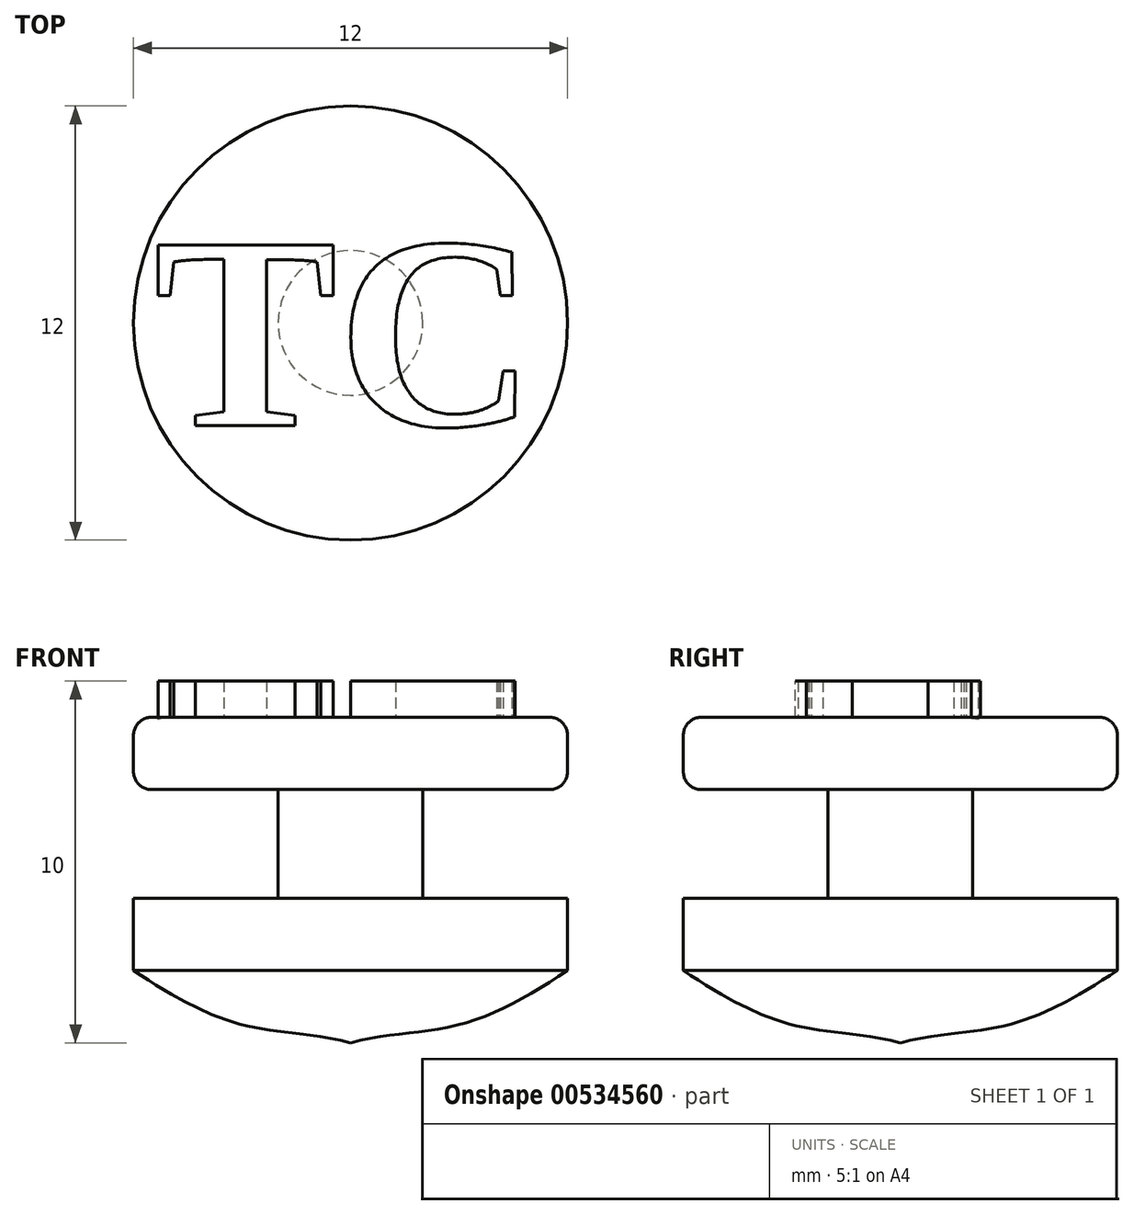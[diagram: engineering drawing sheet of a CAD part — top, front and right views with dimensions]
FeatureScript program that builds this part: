
annotation { "Feature Type Name" : "Feature", "Feature Type Description" : "" }
export const myFeature = defineFeature(function(context is Context, id is Id, definition is map)
    precondition{}
    {
        {
            var Q0;
            Q0=qCreatedBy(makeId("Front.planeOp"),FACE);
            var sketch = newSketch(context, id + "F0", { "sketchPlane" : qUnion([Q0])});
            skLineSegment(sketch, "E0", {"start": v(0, 0) * mm, "end": v(0, 15) * mm});
            skLineSegment(sketch, "E1", {"start": v(0, 15) * mm, "end": v(6, 15) * mm});
            skLineSegment(sketch, "E2", {"start": v(0, 0) * mm, "end": v(0, 4) * mm});
            skLineSegment(sketch, "E3", {"start": v(0, 15) * mm, "end": v(0, 7) * mm});
            skLineSegment(sketch, "E4", {"start": v(0, 7) * mm, "end": v(2, 7) * mm});
            skLineSegment(sketch, "E5.bottom", {"start": v(0, 4) * mm, "end": v(2, 4) * mm});
            skLineSegment(sketch, "E5.left", {"start": v(0, 4) * mm, "end": v(0, 7) * mm});
            skLineSegment(sketch, "E5.right", {"start": v(2, 4) * mm, "end": v(2, 7) * mm});
            skLineSegment(sketch, "E6.left", {"start": v(0, 0) * mm, "end": v(0, 11) * mm});
            skLineSegment(sketch, "E6.right", {"start": v(6, 2) * mm, "end": v(6, 9) * mm});
            skPoint(sketch, "E7.1.internal.snap0", {"position": v(3, 0) * mm});
            skFitSpline(sketch, "E7", {"points": [v(0, 0) * mm, v(3, 0.5) * mm, v(6, 2) * mm], "startDerivative": vector(6.22, 1.73) * mm, "endDerivative": vector(5.79, 3.8) * mm});
            skLineSegment(sketch, "E8", {"start": v(2, 4) * mm, "end": v(6, 4) * mm});
            skPoint(sketch, "E9.orphan", {"position": v(6, 0) * mm});
            skLineSegment(sketch, "E10", {"start": v(2, 7) * mm, "end": v(6, 7) * mm});
            skPoint(sketch, "E11.start.orphan", {"position": v(0, 11) * mm});
            skLineSegment(sketch, "E12", {"start": v(0, 7) * mm, "end": v(0, 11) * mm});
            skLineSegment(sketch, "E13", {"start": v(0, 9) * mm, "end": v(6, 9) * mm});
            skSolve(sketch);
        }
        {
            var Q0;
            {var subQ2=sQuery(id+"F0.wireOp",EDGE,"E5.bottom");Q0=makeQuery(id+"F0.imprint","IMPRINT",FACE,{"disambiguationData":[TD([[makeQuery(id+"F0.imprint","IMPRINT",EDGE,{"derivedFrom":subQ2}),-1.0]])]});}
            var Q1;
            {var subQ0=sQuery(id+"F0.wireOp",EDGE,"E5.bottom");Q1=makeQuery(id+"F0.imprint","IMPRINT",FACE,{"disambiguationData":[TD([[makeQuery(id+"F0.imprint","IMPRINT",EDGE,{"derivedFrom":subQ0}),1.0]])]});}
            var Q2;
            {var subQ4=sQuery(id+"F0.wireOp",EDGE,"E4");Q2=makeQuery(id+"F0.imprint","IMPRINT",FACE,{"disambiguationData":[TD([[makeQuery(id+"F0.imprint","IMPRINT",EDGE,{"derivedFrom":subQ4}),1.0]])]});}
            var Q3;
            Q3=sQuery(id+"F0.wireOp",EDGE,"E6.left");
            revolve(context, id + "F1", {"entities" : qUnion([Q0, Q1, Q2]), "axis" : qUnion([Q3]), "revolveType" : RevolveType.FULL});
        }
        {
            var Q0;
            Q0=makeQuery(id+"F1.opRevolve","SWEPT_FACE",FACE,{"disambiguationData":[OSD([sQuery(id+"F0.wireOp",EDGE,"E13")])]});
            var sketch = newSketch(context, id + "F2", { "sketchPlane" : qUnion([Q0])});
            skText(sketch, "E14", { "text": "TC", "fontName": "Tinos-Bold.ttf"});
            const initialGuessF2  = {"E14": [-0.00544, -0.00283, 1, 0, 0.00548]};
            skSetInitialGuess(sketch, initialGuessF2);
            skSolve(sketch);
        }
        {
            var Q0;
            Q0=makeQuery(id+"F2.imprint","IMPRINT",FACE,{"disambiguationData":[TD([[makeQuery(id+"F2.imprint","IMPRINT",EDGE,{"derivedFrom":sQuery(id+"F2.wireOp",EDGE,"E14.sketch_text.stroke-0")}),-1.0]])]});
            var Q1;
            Q1=makeQuery(id+"F2.imprint","IMPRINT",FACE,{"disambiguationData":[TD([[makeQuery(id+"F2.imprint","IMPRINT",EDGE,{"derivedFrom":sQuery(id+"F2.wireOp",EDGE,"E14.sketch_text.stroke-18")}),-1.0]])]});
            extrude(context, id + "F3", {"entities" : qUnion([Q0, Q1]), "operationType" : NewBodyOperationType.ADD, "depth" : 1 * mm, "offsetDistance" : 25.4 * mm});
        }
        {
            var Q0;
            Q0=makeQuery(id+"F1.opRevolve","SWEPT_EDGE",EDGE,{"disambiguationData":[OSD([sQuery(id+"F0.wireOp",EDGE,"E6.right"),sQuery(id+"F0.wireOp",EDGE,"E10")])]});
            var Q1;
            Q1=makeQuery(id+"F1.opRevolve","SWEPT_EDGE",EDGE,{"disambiguationData":[OSD([sQuery(id+"F0.wireOp",EDGE,"E6.right"),sQuery(id+"F0.wireOp",EDGE,"E13")])]});
            fillet(context, id + "F4", {"entities" : qUnion([Q0, Q1]), "radius" : .5 * mm, "tangentPropagation" : true, "allowEdgeOverflow" : false});
        }
    });
